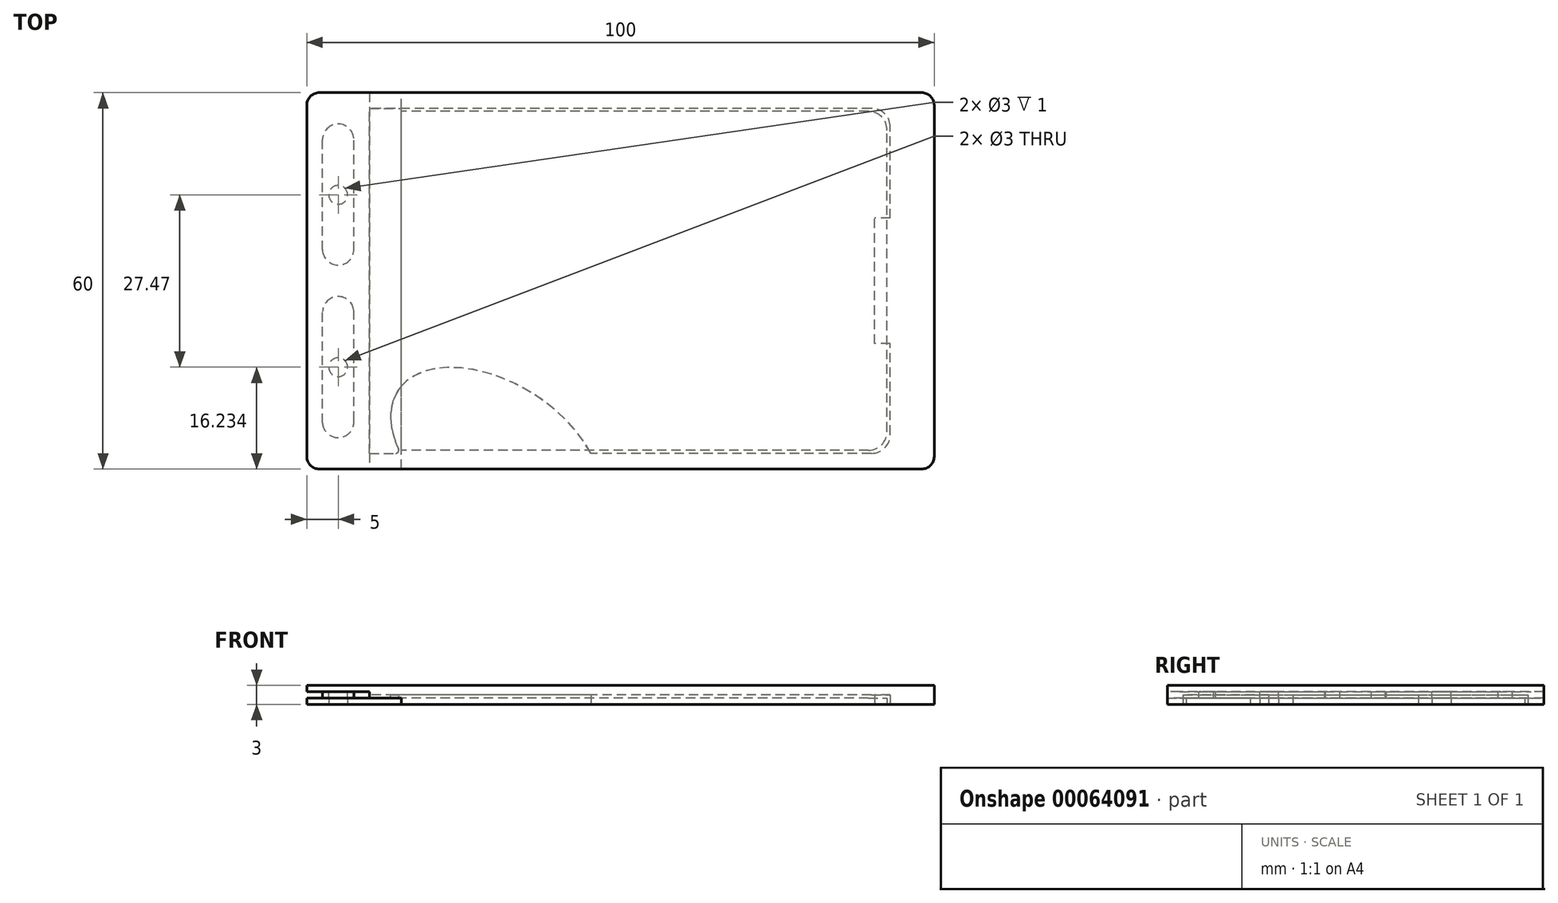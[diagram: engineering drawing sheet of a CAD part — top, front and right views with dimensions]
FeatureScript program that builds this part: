
annotation { "Feature Type Name" : "Feature", "Feature Type Description" : "" }
export const myFeature = defineFeature(function(context is Context, id is Id, definition is map)
    precondition{}
    {
        {
            var Q0;
            Q0=qCreatedBy(makeId("Top.planeOp"),FACE);
            var sketch = newSketch(context, id + "F0", { "sketchPlane" : qUnion([Q0])});
            skLineSegment(sketch, "E0.rect.bottom", {"start": v(39.5, -27) * mm, "end": v(-39.5, -27) * mm});
            skLineSegment(sketch, "E0.rect.top", {"start": v(39.5, 27) * mm, "end": v(-39.5, 27) * mm});
            skLineSegment(sketch, "E0.rect.left", {"start": v(42.5, -24) * mm, "end": v(42.5, 24) * mm});
            skLineSegment(sketch, "E0.rect.right", {"start": v(-42.5, -24) * mm, "end": v(-42.5, 24) * mm});
            skPoint(sketch, "E0.rect.middle", {"position": v(0, 0) * mm});
            skPoint(sketch, "E1.visualSharp", {"position": v(-42.5, 27) * mm});
            skArc(sketch, "E1.filletArc", {"start": v(-39.5, 27) * mm, "mid": v(-41.62, 26.12) * mm, "end": v(-42.5, 24) * mm});
            skPoint(sketch, "E2.visualSharp", {"position": v(-42.5, -27) * mm});
            skArc(sketch, "E2.filletArc", {"start": v(-42.5, -24) * mm, "mid": v(-41.62, -26.12) * mm, "end": v(-39.5, -27) * mm});
            skPoint(sketch, "E3.visualSharp", {"position": v(42.5, -27) * mm});
            skArc(sketch, "E3.filletArc", {"start": v(39.5, -27) * mm, "mid": v(41.62, -26.12) * mm, "end": v(42.5, -24) * mm});
            skPoint(sketch, "E4.visualSharp", {"position": v(42.5, 27) * mm});
            skArc(sketch, "E4.filletArc", {"start": v(42.5, 24) * mm, "mid": v(41.62, 26.12) * mm, "end": v(39.5, 27) * mm});
            skSolve(sketch);
        }
        {
            var Q0;
            Q0=makeQuery(id+"F0.imprint","IMPRINT",FACE,{"disambiguationData":[TD([[makeQuery(id+"F0.imprint","IMPRINT",EDGE,{"derivedFrom":sQuery(id+"F0.wireOp",EDGE,"E0.rect.bottom")}),-1.0]])]});
            extrude(context, id + "F1", {"entities" : qUnion([Q0]), "depth" : 1 * mm});
        }
        {
            var Q0;
            Q0=qCreatedBy(makeId("Top.planeOp"),FACE);
            var sketch = newSketch(context, id + "F2", { "sketchPlane" : qUnion([Q0])});
            skLineSegment(sketch, "E5.rect.bottom", {"start": v(40, -27.5) * mm, "end": v(-4.74, -27.5) * mm});
            skLineSegment(sketch, "E5.rect.top", {"start": v(40, 27.5) * mm, "end": v(-40, 27.5) * mm});
            skLineSegment(sketch, "E5.rect.left", {"start": v(43, -24.5) * mm, "end": v(43, 24.5) * mm});
            skLineSegment(sketch, "E5.rect.right", {"start": v(-43, -24.5) * mm, "end": v(-43, 24.5) * mm});
            skPoint(sketch, "E5.rect.middle", {"position": v(0, 0) * mm});
            skPoint(sketch, "E6.visualSharp", {"position": v(43, 27.5) * mm});
            skArc(sketch, "E6.filletArc", {"start": v(43, 24.5) * mm, "mid": v(42.12, 26.62) * mm, "end": v(40, 27.5) * mm});
            skPoint(sketch, "E7.visualSharp", {"position": v(43, -27.5) * mm});
            skArc(sketch, "E7.filletArc", {"start": v(40, -27.5) * mm, "mid": v(42.12, -26.62) * mm, "end": v(43, -24.5) * mm});
            skPoint(sketch, "E8.visualSharp", {"position": v(-43, -27.5) * mm});
            skArc(sketch, "E8.filletArc", {"start": v(-43, -24.5) * mm, "mid": v(-42.12, -26.62) * mm, "end": v(-40, -27.5) * mm});
            skPoint(sketch, "E9.visualSharp", {"position": v(-43, 27.5) * mm});
            skArc(sketch, "E9.filletArc", {"start": v(-40, 27.5) * mm, "mid": v(-42.12, 26.62) * mm, "end": v(-43, 24.5) * mm});
            skEllipticalArc(sketch, "E10", {});
            skLineSegment(sketch, "E11.trimOffspring", {"start": v(-35.85, -27.5) * mm, "end": v(-40, -27.5) * mm});
            skPoint(sketch, "E12.visualSharp", {"position": v(-35.04, -27.5) * mm});
            skArc(sketch, "E12.filletArc", {"start": v(-35.85, -27.5) * mm, "mid": v(-35.43, -27.27) * mm, "end": v(-35.4, -26.79) * mm});
            skLineSegment(sketch, "E13.rect.bottom", {"start": v(-40.5, -10) * mm, "end": v(-43, -10) * mm});
            skLineSegment(sketch, "E13.rect.top", {"start": v(-40.5, 10) * mm, "end": v(-43, 10) * mm});
            skLineSegment(sketch, "E13.rect.left", {"start": v(-40.5, -10) * mm, "end": v(-40.5, 10) * mm});
            skPoint(sketch, "E13.rect.middle", {"position": v(-43, 0) * mm});
            skLineSegment(sketch, "E14.rect.bottom", {"start": v(43, -10) * mm, "end": v(40.5, -10) * mm});
            skLineSegment(sketch, "E14.rect.top", {"start": v(43, 10) * mm, "end": v(40.5, 10) * mm});
            skLineSegment(sketch, "E14.rect.right", {"start": v(40.5, -10) * mm, "end": v(40.5, 10) * mm});
            skPoint(sketch, "E14.rect.middle", {"position": v(43, 0) * mm});
            skPoint(sketch, "E13.rect.right.end.orphan", {"position": v(-45.5, 10) * mm});
            skPoint(sketch, "E15.orphan", {"position": v(-45.5, -10) * mm});
            skPoint(sketch, "E14.rect.left.end.orphan", {"position": v(45.5, 10) * mm});
            skPoint(sketch, "E16.orphan", {"position": v(45.5, -10) * mm});
            const initialGuessF2  = {"E10": [-0.019889622926712036, -0.0275, 0.8452525898991611, -0.5343669706005046, 0.018514793329349147, 0.011214126226576578, 0.8068131662417332, 3.8965105162049785]};
            skSetInitialGuess(sketch, initialGuessF2);
            skSolve(sketch);
        }
        {
            var Q0;
            Q0=makeQuery(id+"F2.imprint","IMPRINT",FACE,{"disambiguationData":[TD([[makeQuery(id+"F2.imprint","IMPRINT",EDGE,{"derivedFrom":sQuery(id+"F2.wireOp",EDGE,"E5.rect.top")}),1.0]])]});
            extrude(context, id + "F3", {"entities" : qUnion([Q0]), "depth" : 1.5 * mm});
        }
        {
            var Q0;
            Q0=qCreatedBy(makeId("Top.planeOp"),FACE);
            var sketch = newSketch(context, id + "F4", { "sketchPlane" : qUnion([Q0])});
            skLineSegment(sketch, "E17.rect.bottom", {"start": v(50, -30) * mm, "end": v(-50, -30) * mm});
            skLineSegment(sketch, "E17.rect.top", {"start": v(50, 30) * mm, "end": v(-50, 30) * mm});
            skLineSegment(sketch, "E17.rect.left", {"start": v(50, -30) * mm, "end": v(50, 30) * mm});
            skLineSegment(sketch, "E17.rect.right", {"start": v(-50, -30) * mm, "end": v(-50, 30) * mm});
            skPoint(sketch, "E17.rect.middle", {"position": v(0, 0) * mm});
            skLineSegment(sketch, "E18", {"start": v(-40, 30) * mm, "end": v(-40, -30) * mm});
            skSolve(sketch);
        }
        {
            var Q0;
            Q0=makeQuery(id+"F4.imprint","IMPRINT",FACE,{"disambiguationData":[TD([[makeQuery(id+"F4.imprint","IMPRINT",EDGE,{"derivedFrom":sQuery(id+"F4.wireOp",EDGE,"E17.rect.bottom")}),-1.0]])]});
            extrude(context, id + "F5", {"entities" : qUnion([Q0]), "depth" : 3 * mm});
        }
        {
            var Q0;
            Q0=makeQuery(id+"F5.opExtrude","CAP_FACE",FACE,{"disambiguationData":[OSD([sQuery(id+"F4.wireOp",EDGE,"E17.rect.bottom"),sQuery(id+"F4.wireOp",EDGE,"E17.rect.top"),sQuery(id+"F4.wireOp",EDGE,"E17.rect.left"),sQuery(id+"F4.wireOp",EDGE,"E17.rect.right")])],"isStart":false});
            var sketch = newSketch(context, id + "F6", { "sketchPlane" : qUnion([Q0])});
            skLineSegment(sketch, "E19", {"start": v(-45, 30) * mm, "end": v(-45, -30) * mm, "construction": true});
            skLineSegment(sketch, "E20.direction1", {"start": v(-45, 22.5) * mm, "end": v(-20, 22.5) * mm, "construction": true});
            skLineSegment(sketch, "E20.direction2", {"start": v(-45, 22.5) * mm, "end": v(-45, 13.5) * mm, "construction": true});
            skArc(sketch, "E21", {"start": v(-43, 22.5) * mm, "mid": v(-45, 24.5) * mm, "end": v(-47, 22.5) * mm});
            skArc(sketch, "E22", {"start": v(-47, -22.5) * mm, "mid": v(-45, -24.5) * mm, "end": v(-43, -22.5) * mm});
            skLineSegment(sketch, "E23", {"start": v(-47, 22.5) * mm, "end": v(-47, -22.5) * mm});
            skLineSegment(sketch, "E24", {"start": v(-43, 22.5) * mm, "end": v(-43, -22.5) * mm});
            skSolve(sketch);
        }
        {
            var Q0;
            {var subQ0=sQuery(id+"F4.wireOp",EDGE,"E17.rect.right");Q0=makeQuery(id+"F4.imprint","IMPRINT",FACE,{"disambiguationData":[TD([[makeQuery(id+"F4.imprint","IMPRINT",EDGE,{"derivedFrom":subQ0}),-1.0]])]});}
            extrude(context, id + "F7", {"entities" : qUnion([Q0]), "operationType" : NewBodyOperationType.REMOVE, "depth" : 2 * mm});
        }
        {
            var Q0;
            Q0=makeQuery(id+"F7.boolean.opBoolean","COPY",FACE,{"derivedFrom":makeQuery(id+"F7.opExtrude","CAP_FACE",FACE,{"disambiguationData":[OSD([sQuery(id+"F4.wireOp",EDGE,"E17.rect.bottom"),sQuery(id+"F4.wireOp",EDGE,"E17.rect.top"),sQuery(id+"F4.wireOp",EDGE,"E17.rect.right"),sQuery(id+"F4.wireOp",EDGE,"E18")])],"isStart":false})});
            var sketch = newSketch(context, id + "F8", { "sketchPlane" : qUnion([Q0])});
            skLineSegment(sketch, "E25.rect.bottom", {"start": v(-40, -30) * mm, "end": v(-50, -30) * mm});
            skLineSegment(sketch, "E25.rect.top", {"start": v(-40, 30) * mm, "end": v(-50, 30) * mm});
            skLineSegment(sketch, "E25.rect.left", {"start": v(-40, -30) * mm, "end": v(-40, 30) * mm});
            skLineSegment(sketch, "E25.rect.right", {"start": v(-50, -30) * mm, "end": v(-50, 30) * mm});
            skPoint(sketch, "E25.rect.middle", {"position": v(-45, 0) * mm});
            skPoint(sketch, "E25.rect.middle.positionSnap0", {"position": v(-45, 30) * mm});
            skPoint(sketch, "E25.rect.centerSnap0", {"position": v(-45, 30) * mm});
            skArc(sketch, "E26", {"start": v(-42.5, 22.28) * mm, "mid": v(-44.96, 25) * mm, "end": v(-47.5, 22.35) * mm});
            skArc(sketch, "E27", {"start": v(-47.5, -22.5) * mm, "mid": v(-44.89, -25) * mm, "end": v(-42.5, -22.28) * mm});
            skLineSegment(sketch, "E28", {"start": v(-47.5, 22.65) * mm, "end": v(-47.5, 4.89) * mm});
            skLineSegment(sketch, "E29", {"start": v(-42.5, 22.28) * mm, "end": v(-42.5, 4.78) * mm});
            skArc(sketch, "E30", {"start": v(-42.5, -5.22) * mm, "mid": v(-44.93, -2.5) * mm, "end": v(-47.5, -5.1) * mm});
            skArc(sketch, "E31", {"start": v(-47.5, 5.12) * mm, "mid": v(-44.95, 2.5) * mm, "end": v(-42.5, 5.22) * mm});
            skLineSegment(sketch, "E32.trimOffspring", {"start": v(-42.5, -4.78) * mm, "end": v(-42.5, -22.72) * mm});
            skLineSegment(sketch, "E33.trimOffspring", {"start": v(-47.5, -4.9) * mm, "end": v(-47.5, -22.5) * mm});
            skCircle(sketch, "E34", {"center": v(-45, 13.77) * mm, "radius": 1.5 * mm});
            skPoint(sketch, "E34.centerSnap0", {"position": v(-47.5, 13.77) * mm});
            skCircle(sketch, "E35", {"center": v(-45, -13.7) * mm, "radius": 1.5 * mm});
            skPoint(sketch, "E35.centerSnap0", {"position": v(-47.5, -13.7) * mm});
            skSolve(sketch);
        }
        {
            var Q0;
            {var subQ1=sQuery(id+"F8.wireOp",EDGE,"E26");var subQ6=sQuery(id+"F8.wireOp",EDGE,"E29");var subQ8=makeQuery(id+"F8.imprint","INTERSECT",VERTEX,{"derivedFrom":[subQ1,subQ6]});Q0=makeQuery(id+"F8.imprint","IMPRINT",FACE,{"disambiguationData":[TD([[makeQuery(id+"F8.imprint","IMPRINT",EDGE,{"disambiguationData":[TD([[subQ8,-1.0]])],"derivedFrom":subQ1}),1.0]])]});}
            var Q1;
            {var subQ4=sQuery(id+"F8.wireOp",EDGE,"E33.trimOffspring");var subQ6=sQuery(id+"F8.wireOp",EDGE,"E27");var subQ8=makeQuery(id+"F8.imprint","INTERSECT",VERTEX,{"derivedFrom":[subQ6,subQ4]});Q1=makeQuery(id+"F8.imprint","IMPRINT",FACE,{"disambiguationData":[TD([[makeQuery(id+"F8.imprint","IMPRINT",EDGE,{"disambiguationData":[TD([[subQ8,-1.0]])],"derivedFrom":subQ6}),1.0]])]});}
            extrude(context, id + "F9", {"entities" : qUnion([Q0, Q1]), "operationType" : NewBodyOperationType.ADD, "depth" : 1 * mm});
        }
        {
            var Q0;
            Q0=makeQuery(id+"F5.opExtrude","CAP_FACE",FACE,{"disambiguationData":[OSD([sQuery(id+"F4.wireOp",EDGE,"E17.rect.bottom"),sQuery(id+"F4.wireOp",EDGE,"E17.rect.top"),sQuery(id+"F4.wireOp",EDGE,"E17.rect.left"),sQuery(id+"F4.wireOp",EDGE,"E17.rect.right")])],"isStart":true});
            var sketch = newSketch(context, id + "F10", { "sketchPlane" : qUnion([Q0])});
            skLineSegment(sketch, "E36.0", {"start": v(-50, 30) * mm, "end": v(-50, -30) * mm});
            skCircle(sketch, "E37.0", {"center": v(-45, 13.77) * mm, "radius": 1.5 * mm});
            skCircle(sketch, "E38.0", {"center": v(-45, -13.7) * mm, "radius": 1.5 * mm});
            skLineSegment(sketch, "E39", {"start": v(-48.5, 31.53) * mm, "end": v(-48.5, -33.85) * mm, "construction": true});
            skLineSegment(sketch, "E40.0", {"start": v(-40, 30) * mm, "end": v(-50, 30) * mm});
            skLineSegment(sketch, "E41.0", {"start": v(-40, -30) * mm, "end": v(-50, -30) * mm});
            skLineSegment(sketch, "E42.bottom", {"start": v(-48.5, 30) * mm, "end": v(-34.9, 30) * mm});
            skLineSegment(sketch, "E42.top", {"start": v(-48.5, -30) * mm, "end": v(-34.9, -30) * mm});
            skLineSegment(sketch, "E42.left", {"start": v(-48.5, 30) * mm, "end": v(-48.5, -30) * mm});
            skLineSegment(sketch, "E42.right", {"start": v(-34.9, 30) * mm, "end": v(-34.9, -30) * mm});
            skSolve(sketch);
        }
        {
            var Q0;
            {var subQ2=sQuery(id+"F10.wireOp",EDGE,"E42.right");Q0=makeQuery(id+"F10.imprint","IMPRINT",FACE,{"disambiguationData":[TD([[makeQuery(id+"F10.imprint","IMPRINT",EDGE,{"derivedFrom":subQ2}),-1.0]])]});}
            extrude(context, id + "F11", {"entities" : qUnion([Q0]), "operationType" : NewBodyOperationType.REMOVE, "oppositeDirection" : true, "depth" : 1 * mm});
        }
        {
            var Q0;
            Q0 = qSketchRegion(id + "F10", true);
            extrude(context, id + "F12", {"entities" : qUnion([Q0]), "oppositeDirection" : true, "depth" : 1 * mm});
        }
        {
            var Q0;
            Q0=makeQuery(id+"F5.opExtrude","SWEPT_EDGE",EDGE,{"disambiguationData":[OSD([sQuery(id+"F4.wireOp",EDGE,"E17.rect.bottom"),sQuery(id+"F4.wireOp",EDGE,"E17.rect.right")])]});
            var Q1;
            Q1=makeQuery(id+"F12.opExtrude","SWEPT_EDGE",EDGE,{"disambiguationData":[OSD([sQuery(id+"F10.wireOp",EDGE,"E36.0"),sQuery(id+"F10.wireOp",EDGE,"E40.0")])]});
            var Q2;
            Q2=makeQuery(id+"F12.opExtrude","SWEPT_EDGE",EDGE,{"disambiguationData":[OSD([sQuery(id+"F10.wireOp",EDGE,"E36.0"),sQuery(id+"F10.wireOp",EDGE,"E41.0")])]});
            var Q3;
            Q3=makeQuery(id+"F5.opExtrude","SWEPT_EDGE",EDGE,{"disambiguationData":[OSD([sQuery(id+"F4.wireOp",EDGE,"E17.rect.top"),sQuery(id+"F4.wireOp",EDGE,"E17.rect.right")])]});
            var Q4;
            Q4=makeQuery(id+"F5.opExtrude","SWEPT_EDGE",EDGE,{"disambiguationData":[OSD([sQuery(id+"F4.wireOp",EDGE,"E17.rect.top"),sQuery(id+"F4.wireOp",EDGE,"E17.rect.left")])]});
            var Q5;
            Q5=makeQuery(id+"F5.opExtrude","SWEPT_EDGE",EDGE,{"disambiguationData":[OSD([sQuery(id+"F4.wireOp",EDGE,"E17.rect.bottom"),sQuery(id+"F4.wireOp",EDGE,"E17.rect.left")])]});
            fillet(context, id + "F13", {"entities" : qUnion([Q0, Q1, Q2, Q3, Q4, Q5]), "radius" : 2 * mm, "tangentPropagation" : true, "allowEdgeOverflow" : false});
        }
    });
